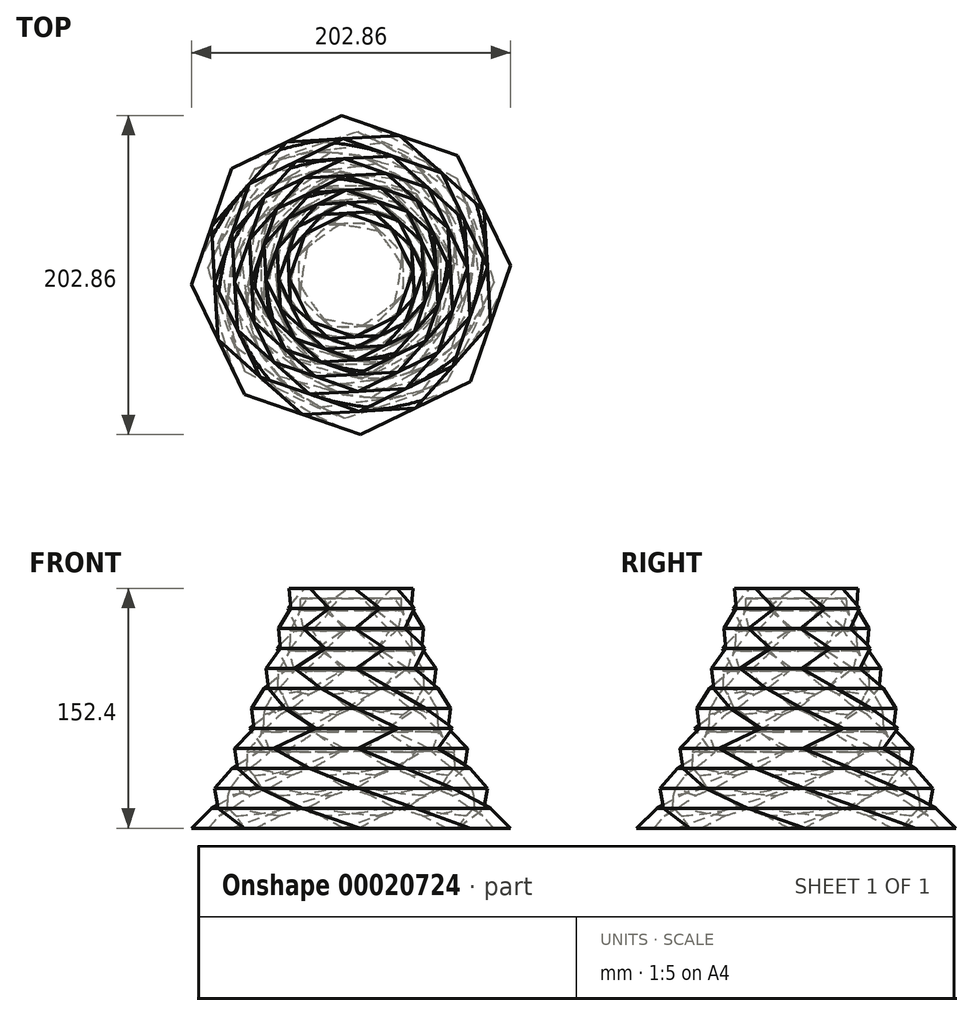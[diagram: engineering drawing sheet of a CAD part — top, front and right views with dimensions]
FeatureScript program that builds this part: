
annotation { "Feature Type Name" : "Feature", "Feature Type Description" : "" }
export const myFeature = defineFeature(function(context is Context, id is Id, definition is map)
    precondition{}
    {
        {
            var Q0;
            Q0=qCreatedBy(makeId("Top.planeOp"),FACE);
            var sketch = newSketch(context, id + "F0", { "sketchPlane" : qUnion([Q0])});
            skCircle(sketch, "E0.cCircle", {"center": v(0, 0) * mm, "radius": 101.6 * mm, "construction": true});
            skLineSegment(sketch, "E0.0", {"start": v(-5.9, 101.43) * mm, "end": v(67.56, 75.89) * mm});
            skLineSegment(sketch, "E0.1", {"start": v(67.56, 75.89) * mm, "end": v(101.43, 5.9) * mm});
            skLineSegment(sketch, "E0.2", {"start": v(101.43, 5.9) * mm, "end": v(75.89, -67.56) * mm});
            skLineSegment(sketch, "E0.3", {"start": v(75.89, -67.56) * mm, "end": v(5.9, -101.43) * mm});
            skLineSegment(sketch, "E0.4", {"start": v(5.9, -101.43) * mm, "end": v(-67.56, -75.89) * mm});
            skLineSegment(sketch, "E0.5", {"start": v(-67.56, -75.89) * mm, "end": v(-101.43, -5.9) * mm});
            skLineSegment(sketch, "E0.6", {"start": v(-101.43, -5.9) * mm, "end": v(-75.89, 67.56) * mm});
            skLineSegment(sketch, "E0.7", {"start": v(-75.89, 67.56) * mm, "end": v(-5.9, 101.43) * mm});
            skSolve(sketch);
        }
        {
            var Q0;
            Q0=qCreatedBy(makeId("Top.planeOp"),FACE);
            cPlane(context, id + "F1", {"entities" : qUnion([Q0]), "cplaneType" : CPlaneType.OFFSET, "offset" : 12.7 * mm, "width" : 152.4 * mm, "height" : 152.4 * mm});
        }
        {
            var Q0;
            Q0=qCreatedBy(id+"F1.planeOp",FACE);
            var sketch = newSketch(context, id + "F2", { "sketchPlane" : qUnion([Q0])});
            skPoint(sketch, "E1.0", {"position": v(-101.43, -5.9) * mm});
            skPoint(sketch, "E2.0", {"position": v(-88.66, 30.83) * mm});
            skCircle(sketch, "E3.cCircle", {"center": v(0, 0) * mm, "radius": 93.87 * mm, "construction": true});
            skLineSegment(sketch, "E3.0", {"start": v(-88.66, 30.83) * mm, "end": v(-40.89, 84.5) * mm});
            skLineSegment(sketch, "E3.1", {"start": v(-40.89, 84.5) * mm, "end": v(30.83, 88.66) * mm});
            skLineSegment(sketch, "E3.2", {"start": v(30.83, 88.66) * mm, "end": v(84.5, 40.89) * mm});
            skLineSegment(sketch, "E3.3", {"start": v(84.5, 40.89) * mm, "end": v(88.66, -30.83) * mm});
            skLineSegment(sketch, "E3.4", {"start": v(88.66, -30.83) * mm, "end": v(40.89, -84.5) * mm});
            skLineSegment(sketch, "E3.5", {"start": v(40.89, -84.5) * mm, "end": v(-30.83, -88.66) * mm});
            skLineSegment(sketch, "E3.6", {"start": v(-30.83, -88.66) * mm, "end": v(-84.5, -40.89) * mm});
            skLineSegment(sketch, "E3.7", {"start": v(-84.5, -40.89) * mm, "end": v(-88.66, 30.83) * mm});
            skSolve(sketch);
        }
        {
            var Q0;
            Q0=makeQuery(id+"F0.imprint","IMPRINT",FACE,{"disambiguationData":[TD([[makeQuery(id+"F0.imprint","IMPRINT",EDGE,{"derivedFrom":sQuery(id+"F0.wireOp",EDGE,"E0.0")}),-1.0]])]});
            var Q1;
            Q1=makeQuery(id+"F2.imprint","IMPRINT",FACE,{"disambiguationData":[TD([[makeQuery(id+"F2.imprint","IMPRINT",EDGE,{"derivedFrom":sQuery(id+"F2.wireOp",EDGE,"E3.0")}),-1.0]])]});
            loft(context, id + "F3", {"sheetProfilesArray" : [{ "sheetProfileEntities" : qUnion([Q0]) }, { "sheetProfileEntities" : qUnion([Q1]) }]});
        }
        {
            var Q0;
            Q0=qCreatedBy(id+"F1.planeOp",FACE);
            cPlane(context, id + "F4", {"entities" : qUnion([Q0]), "cplaneType" : CPlaneType.OFFSET, "offset" : 12.7 * mm, "width" : 152.4 * mm, "height" : 152.4 * mm});
        }
        {
            var Q0;
            Q0=qCreatedBy(id+"F4.planeOp",FACE);
            var sketch = newSketch(context, id + "F5", { "sketchPlane" : qUnion([Q0])});
            skPoint(sketch, "E4.0", {"position": v(0, 0) * mm});
            skPoint(sketch, "E5.0", {"position": v(-86.58, -5.03) * mm});
            skPoint(sketch, "E6.0", {"position": v(-57.66, -64.77) * mm});
            skPoint(sketch, "E7.0", {"position": v(-88.66, 30.83) * mm});
            skCircle(sketch, "E8.cCircle", {"center": v(0, 0) * mm, "radius": 86.72 * mm, "construction": true});
            skLineSegment(sketch, "E8.0", {"start": v(-57.66, -64.77) * mm, "end": v(-86.58, -5.03) * mm});
            skLineSegment(sketch, "E8.1", {"start": v(-86.58, -5.03) * mm, "end": v(-64.77, 57.66) * mm});
            skLineSegment(sketch, "E8.2", {"start": v(-64.77, 57.66) * mm, "end": v(-5.03, 86.58) * mm});
            skLineSegment(sketch, "E8.3", {"start": v(-5.03, 86.58) * mm, "end": v(57.66, 64.77) * mm});
            skLineSegment(sketch, "E8.4", {"start": v(57.66, 64.77) * mm, "end": v(86.58, 5.03) * mm});
            skLineSegment(sketch, "E8.5", {"start": v(86.58, 5.03) * mm, "end": v(64.77, -57.66) * mm});
            skLineSegment(sketch, "E8.6", {"start": v(64.77, -57.66) * mm, "end": v(5.03, -86.58) * mm});
            skLineSegment(sketch, "E8.7", {"start": v(5.03, -86.58) * mm, "end": v(-57.66, -64.77) * mm});
            skSolve(sketch);
        }
        {
            var Q1;
            Q1=makeQuery(id+"F3.opLoft","CAP_FACE",FACE,{"disambiguationData":[OSD([makeQuery(id+"F2.imprint","IMPRINT",FACE,{"disambiguationData":[TD([[makeQuery(id+"F2.imprint","IMPRINT",EDGE,{"derivedFrom":sQuery(id+"F2.wireOp",EDGE,"E3.0")}),-1.0]])]})])],"isStart":true});
            var Q2;
            Q2=makeQuery(id+"F5.imprint","IMPRINT",FACE,{"disambiguationData":[TD([[makeQuery(id+"F5.imprint","IMPRINT",EDGE,{"derivedFrom":sQuery(id+"F5.wireOp",EDGE,"E8.0")}),-1.0]])]});
            loft(context, id + "F6", {"operationType" : NewBodyOperationType.ADD, "sheetProfilesArray" : [{ "sheetProfileEntities" : qUnion([Q1]) }, { "sheetProfileEntities" : qUnion([Q2]) }]});
        }
        {
            var Q0;
            Q0=qCreatedBy(id+"F4.planeOp",FACE);
            cPlane(context, id + "F7", {"entities" : qUnion([Q0]), "cplaneType" : CPlaneType.OFFSET, "offset" : 12.7 * mm, "width" : 152.4 * mm, "height" : 152.4 * mm});
        }
        {
            var Q0;
            Q0=qCreatedBy(id+"F7.planeOp",FACE);
            var sketch = newSketch(context, id + "F8", { "sketchPlane" : qUnion([Q0])});
            skPoint(sketch, "E9.0", {"position": v(26.32, 75.67) * mm});
            skPoint(sketch, "E10.0", {"position": v(0, 0) * mm});
            skCircle(sketch, "E11.cCircle", {"center": v(0, 0) * mm, "radius": 80.12 * mm, "construction": true});
            skLineSegment(sketch, "E11.0", {"start": v(26.32, 75.67) * mm, "end": v(72.12, 34.9) * mm});
            skLineSegment(sketch, "E11.1", {"start": v(72.12, 34.9) * mm, "end": v(75.67, -26.32) * mm});
            skLineSegment(sketch, "E11.2", {"start": v(75.67, -26.32) * mm, "end": v(34.9, -72.12) * mm});
            skLineSegment(sketch, "E11.3", {"start": v(34.9, -72.12) * mm, "end": v(-26.32, -75.67) * mm});
            skLineSegment(sketch, "E11.4", {"start": v(-26.32, -75.67) * mm, "end": v(-72.12, -34.9) * mm});
            skLineSegment(sketch, "E11.5", {"start": v(-72.12, -34.9) * mm, "end": v(-75.67, 26.32) * mm});
            skLineSegment(sketch, "E11.6", {"start": v(-75.67, 26.32) * mm, "end": v(-34.9, 72.12) * mm});
            skLineSegment(sketch, "E11.7", {"start": v(-34.9, 72.12) * mm, "end": v(26.32, 75.67) * mm});
            skSolve(sketch);
        }
        {
            var Q1;
            Q1=makeQuery(id+"F6.opLoft","CAP_FACE",FACE,{"disambiguationData":[OSD([makeQuery(id+"F5.imprint","IMPRINT",FACE,{"disambiguationData":[TD([[makeQuery(id+"F5.imprint","IMPRINT",EDGE,{"derivedFrom":sQuery(id+"F5.wireOp",EDGE,"E8.0")}),-1.0]])]})])],"isStart":true});
            var Q2;
            Q2=makeQuery(id+"F8.imprint","IMPRINT",FACE,{"disambiguationData":[TD([[makeQuery(id+"F8.imprint","IMPRINT",EDGE,{"derivedFrom":sQuery(id+"F8.wireOp",EDGE,"E11.0")}),-1.0]])]});
            loft(context, id + "F9", {"operationType" : NewBodyOperationType.ADD, "sheetProfilesArray" : [{ "sheetProfileEntities" : qUnion([Q1]) }, { "sheetProfileEntities" : qUnion([Q2]) }]});
        }
        {
            var Q0;
            Q0=qCreatedBy(id+"F7.planeOp",FACE);
            cPlane(context, id + "F10", {"entities" : qUnion([Q0]), "cplaneType" : CPlaneType.OFFSET, "offset" : 12.7 * mm, "width" : 152.4 * mm, "height" : 152.4 * mm});
        }
        {
            var Q0;
            Q0=qCreatedBy(id+"F10.planeOp",FACE);
            var sketch = newSketch(context, id + "F11", { "sketchPlane" : qUnion([Q0])});
            skPoint(sketch, "E12.0", {"position": v(0, 0) * mm});
            skPoint(sketch, "E13.0", {"position": v(4.3, -73.9) * mm});
            skCircle(sketch, "E14.cCircle", {"center": v(0, 0) * mm, "radius": 74.02 * mm, "construction": true});
            skLineSegment(sketch, "E14.0", {"start": v(4.3, -73.9) * mm, "end": v(-49.22, -55.29) * mm});
            skLineSegment(sketch, "E14.1", {"start": v(-49.22, -55.29) * mm, "end": v(-73.9, -4.3) * mm});
            skLineSegment(sketch, "E14.2", {"start": v(-73.9, -4.3) * mm, "end": v(-55.29, 49.22) * mm});
            skLineSegment(sketch, "E14.3", {"start": v(-55.29, 49.22) * mm, "end": v(-4.3, 73.9) * mm});
            skLineSegment(sketch, "E14.4", {"start": v(-4.3, 73.9) * mm, "end": v(49.22, 55.29) * mm});
            skLineSegment(sketch, "E14.5", {"start": v(49.22, 55.29) * mm, "end": v(73.9, 4.3) * mm});
            skLineSegment(sketch, "E14.6", {"start": v(73.9, 4.3) * mm, "end": v(55.29, -49.22) * mm});
            skLineSegment(sketch, "E14.7", {"start": v(55.29, -49.22) * mm, "end": v(4.3, -73.9) * mm});
            skSolve(sketch);
        }
        {
            var Q1;
            Q1=makeQuery(id+"F9.opLoft","CAP_FACE",FACE,{"disambiguationData":[OSD([makeQuery(id+"F8.imprint","IMPRINT",FACE,{"disambiguationData":[TD([[makeQuery(id+"F8.imprint","IMPRINT",EDGE,{"derivedFrom":sQuery(id+"F8.wireOp",EDGE,"E11.0")}),-1.0]])]})])],"isStart":true});
            var Q2;
            Q2=makeQuery(id+"F11.imprint","IMPRINT",FACE,{"disambiguationData":[TD([[makeQuery(id+"F11.imprint","IMPRINT",EDGE,{"derivedFrom":sQuery(id+"F11.wireOp",EDGE,"E14.0")}),-1.0]])]});
            loft(context, id + "F12", {"operationType" : NewBodyOperationType.ADD, "sheetProfilesArray" : [{ "sheetProfileEntities" : qUnion([Q1]) }, { "sheetProfileEntities" : qUnion([Q2]) }]});
        }
        {
            var Q0;
            Q0=qCreatedBy(id+"F10.planeOp",FACE);
            cPlane(context, id + "F13", {"entities" : qUnion([Q0]), "cplaneType" : CPlaneType.OFFSET, "offset" : 12.7 * mm, "width" : 152.4 * mm, "height" : 152.4 * mm});
        }
        {
            var Q0;
            Q0=qCreatedBy(id+"F13.planeOp",FACE);
            var sketch = newSketch(context, id + "F14", { "sketchPlane" : qUnion([Q0])});
            skPoint(sketch, "E15.0", {"position": v(0, 0) * mm});
            skPoint(sketch, "E16.0", {"position": v(-22.46, -64.6) * mm});
            skCircle(sketch, "E17.cCircle", {"center": v(0, 0) * mm, "radius": 68.39 * mm, "construction": true});
            skLineSegment(sketch, "E17.0", {"start": v(-22.46, -64.6) * mm, "end": v(-61.56, -29.79) * mm});
            skLineSegment(sketch, "E17.1", {"start": v(-61.56, -29.79) * mm, "end": v(-64.6, 22.46) * mm});
            skLineSegment(sketch, "E17.2", {"start": v(-64.6, 22.46) * mm, "end": v(-29.79, 61.56) * mm});
            skLineSegment(sketch, "E17.3", {"start": v(-29.79, 61.56) * mm, "end": v(22.46, 64.6) * mm});
            skLineSegment(sketch, "E17.4", {"start": v(22.46, 64.6) * mm, "end": v(61.56, 29.79) * mm});
            skLineSegment(sketch, "E17.5", {"start": v(61.56, 29.79) * mm, "end": v(64.6, -22.46) * mm});
            skLineSegment(sketch, "E17.6", {"start": v(64.6, -22.46) * mm, "end": v(29.79, -61.56) * mm});
            skLineSegment(sketch, "E17.7", {"start": v(29.79, -61.56) * mm, "end": v(-22.46, -64.6) * mm});
            skSolve(sketch);
        }
        {
            var Q1;
            Q1=makeQuery(id+"F12.opLoft","CAP_FACE",FACE,{"disambiguationData":[OSD([makeQuery(id+"F11.imprint","IMPRINT",FACE,{"disambiguationData":[TD([[makeQuery(id+"F11.imprint","IMPRINT",EDGE,{"derivedFrom":sQuery(id+"F11.wireOp",EDGE,"E14.0")}),-1.0]])]})])],"isStart":true});
            var Q2;
            Q2=makeQuery(id+"F14.imprint","IMPRINT",FACE,{"disambiguationData":[TD([[makeQuery(id+"F14.imprint","IMPRINT",EDGE,{"derivedFrom":sQuery(id+"F14.wireOp",EDGE,"E17.0")}),-1.0]])]});
            loft(context, id + "F15", {"operationType" : NewBodyOperationType.ADD, "sheetProfilesArray" : [{ "sheetProfileEntities" : qUnion([Q1]) }, { "sheetProfileEntities" : qUnion([Q2]) }]});
        }
        {
            var Q0;
            Q0=qCreatedBy(id+"F13.planeOp",FACE);
            cPlane(context, id + "F16", {"entities" : qUnion([Q0]), "cplaneType" : CPlaneType.OFFSET, "offset" : 12.7 * mm, "width" : 152.4 * mm, "height" : 152.4 * mm});
        }
        {
            var Q0;
            Q0=qCreatedBy(id+"F16.planeOp",FACE);
            var sketch = newSketch(context, id + "F17", { "sketchPlane" : qUnion([Q0])});
            skPoint(sketch, "E18.0", {"position": v(0, 0) * mm});
            skPoint(sketch, "E19.0", {"position": v(3.66, -63.07) * mm});
            skCircle(sketch, "E20.cCircle", {"center": v(0, 0) * mm, "radius": 63.18 * mm, "construction": true});
            skLineSegment(sketch, "E20.0", {"start": v(3.66, -63.07) * mm, "end": v(-42, -47.2) * mm});
            skLineSegment(sketch, "E20.1", {"start": v(-42, -47.2) * mm, "end": v(-63.07, -3.66) * mm});
            skLineSegment(sketch, "E20.2", {"start": v(-63.07, -3.66) * mm, "end": v(-47.2, 42) * mm});
            skLineSegment(sketch, "E20.3", {"start": v(-47.2, 42) * mm, "end": v(-3.66, 63.07) * mm});
            skLineSegment(sketch, "E20.4", {"start": v(-3.66, 63.07) * mm, "end": v(42, 47.2) * mm});
            skLineSegment(sketch, "E20.5", {"start": v(42, 47.2) * mm, "end": v(63.07, 3.66) * mm});
            skLineSegment(sketch, "E20.6", {"start": v(63.07, 3.66) * mm, "end": v(47.2, -42) * mm});
            skLineSegment(sketch, "E20.7", {"start": v(47.2, -42) * mm, "end": v(3.66, -63.07) * mm});
            skSolve(sketch);
        }
        {
            var Q1;
            Q1=makeQuery(id+"F15.opLoft","CAP_FACE",FACE,{"disambiguationData":[OSD([makeQuery(id+"F14.imprint","IMPRINT",FACE,{"disambiguationData":[TD([[makeQuery(id+"F14.imprint","IMPRINT",EDGE,{"derivedFrom":sQuery(id+"F14.wireOp",EDGE,"E17.0")}),-1.0]])]})])],"isStart":true});
            var Q2;
            Q2=makeQuery(id+"F17.imprint","IMPRINT",FACE,{"disambiguationData":[TD([[makeQuery(id+"F17.imprint","IMPRINT",EDGE,{"derivedFrom":sQuery(id+"F17.wireOp",EDGE,"E20.0")}),-1.0]])]});
            loft(context, id + "F18", {"operationType" : NewBodyOperationType.ADD, "sheetProfilesArray" : [{ "sheetProfileEntities" : qUnion([Q1]) }, { "sheetProfileEntities" : qUnion([Q2]) }]});
        }
        {
            var Q0;
            Q0=qCreatedBy(id+"F16.planeOp",FACE);
            cPlane(context, id + "F19", {"entities" : qUnion([Q0]), "cplaneType" : CPlaneType.OFFSET, "offset" : 12.7 * mm, "width" : 152.4 * mm, "height" : 152.4 * mm});
        }
        {
            var Q0;
            Q0=qCreatedBy(id+"F19.planeOp",FACE);
            var sketch = newSketch(context, id + "F20", { "sketchPlane" : qUnion([Q0])});
            skPoint(sketch, "E21.0", {"position": v(0, 0) * mm});
            skPoint(sketch, "E22.0", {"position": v(25.43, -52.54) * mm});
            skCircle(sketch, "E23.cCircle", {"center": v(0, 0) * mm, "radius": 58.37 * mm, "construction": true});
            skLineSegment(sketch, "E23.0", {"start": v(25.43, -52.54) * mm, "end": v(-19.17, -55.13) * mm});
            skLineSegment(sketch, "E23.1", {"start": v(-19.17, -55.13) * mm, "end": v(-52.54, -25.43) * mm});
            skLineSegment(sketch, "E23.2", {"start": v(-52.54, -25.43) * mm, "end": v(-55.13, 19.17) * mm});
            skLineSegment(sketch, "E23.3", {"start": v(-55.13, 19.17) * mm, "end": v(-25.43, 52.54) * mm});
            skLineSegment(sketch, "E23.4", {"start": v(-25.43, 52.54) * mm, "end": v(19.17, 55.13) * mm});
            skLineSegment(sketch, "E23.5", {"start": v(19.17, 55.13) * mm, "end": v(52.54, 25.43) * mm});
            skLineSegment(sketch, "E23.6", {"start": v(52.54, 25.43) * mm, "end": v(55.13, -19.17) * mm});
            skLineSegment(sketch, "E23.7", {"start": v(55.13, -19.17) * mm, "end": v(25.43, -52.54) * mm});
            skSolve(sketch);
        }
        {
            var Q1;
            Q1=makeQuery(id+"F18.opLoft","CAP_FACE",FACE,{"disambiguationData":[OSD([makeQuery(id+"F17.imprint","IMPRINT",FACE,{"disambiguationData":[TD([[makeQuery(id+"F17.imprint","IMPRINT",EDGE,{"derivedFrom":sQuery(id+"F17.wireOp",EDGE,"E20.0")}),-1.0]])]})])],"isStart":true});
            var Q2;
            Q2=makeQuery(id+"F20.imprint","IMPRINT",FACE,{"disambiguationData":[TD([[makeQuery(id+"F20.imprint","IMPRINT",EDGE,{"derivedFrom":sQuery(id+"F20.wireOp",EDGE,"E23.0")}),-1.0]])]});
            loft(context, id + "F21", {"operationType" : NewBodyOperationType.ADD, "sheetProfilesArray" : [{ "sheetProfileEntities" : qUnion([Q1]) }, { "sheetProfileEntities" : qUnion([Q2]) }]});
        }
        {
            var Q0;
            Q0=qCreatedBy(id+"F19.planeOp",FACE);
            cPlane(context, id + "F22", {"entities" : qUnion([Q0]), "cplaneType" : CPlaneType.OFFSET, "offset" : 12.7 * mm, "width" : 152.4 * mm, "height" : 152.4 * mm});
        }
        {
            var Q0;
            Q0=qCreatedBy(id+"F22.planeOp",FACE);
            var sketch = newSketch(context, id + "F23", { "sketchPlane" : qUnion([Q0])});
            skPoint(sketch, "E24.0", {"position": v(0, 0) * mm});
            skPoint(sketch, "E25.0", {"position": v(3.13, -53.84) * mm});
            skCircle(sketch, "E26.cCircle", {"center": v(0, 0) * mm, "radius": 53.93 * mm, "construction": true});
            skLineSegment(sketch, "E26.0", {"start": v(3.13, -53.84) * mm, "end": v(-35.86, -40.28) * mm});
            skLineSegment(sketch, "E26.1", {"start": v(-35.86, -40.28) * mm, "end": v(-53.84, -3.13) * mm});
            skLineSegment(sketch, "E26.2", {"start": v(-53.84, -3.13) * mm, "end": v(-40.28, 35.86) * mm});
            skLineSegment(sketch, "E26.3", {"start": v(-40.28, 35.86) * mm, "end": v(-3.13, 53.84) * mm});
            skLineSegment(sketch, "E26.4", {"start": v(-3.13, 53.84) * mm, "end": v(35.86, 40.28) * mm});
            skLineSegment(sketch, "E26.5", {"start": v(35.86, 40.28) * mm, "end": v(53.84, 3.13) * mm});
            skLineSegment(sketch, "E26.6", {"start": v(53.84, 3.13) * mm, "end": v(40.28, -35.86) * mm});
            skLineSegment(sketch, "E26.7", {"start": v(40.28, -35.86) * mm, "end": v(3.13, -53.84) * mm});
            skSolve(sketch);
        }
        {
            var Q1;
            Q1=makeQuery(id+"F21.opLoft","CAP_FACE",FACE,{"disambiguationData":[OSD([makeQuery(id+"F20.imprint","IMPRINT",FACE,{"disambiguationData":[TD([[makeQuery(id+"F20.imprint","IMPRINT",EDGE,{"derivedFrom":sQuery(id+"F20.wireOp",EDGE,"E23.0")}),-1.0]])]})])],"isStart":true});
            var Q2;
            Q2=makeQuery(id+"F23.imprint","IMPRINT",FACE,{"disambiguationData":[TD([[makeQuery(id+"F23.imprint","IMPRINT",EDGE,{"derivedFrom":sQuery(id+"F23.wireOp",EDGE,"E26.0")}),-1.0]])]});
            loft(context, id + "F24", {"operationType" : NewBodyOperationType.ADD, "sheetProfilesArray" : [{ "sheetProfileEntities" : qUnion([Q1]) }, { "sheetProfileEntities" : qUnion([Q2]) }]});
        }
        {
            var Q0;
            Q0=qCreatedBy(id+"F22.planeOp",FACE);
            cPlane(context, id + "F25", {"entities" : qUnion([Q0]), "cplaneType" : CPlaneType.OFFSET, "offset" : 12.7 * mm, "width" : 152.4 * mm, "height" : 152.4 * mm});
        }
        {
            var Q0;
            Q0=qCreatedBy(id+"F25.planeOp",FACE);
            var sketch = newSketch(context, id + "F26", { "sketchPlane" : qUnion([Q0])});
            skPoint(sketch, "E27.0", {"position": v(0, 0) * mm});
            skPoint(sketch, "E28.0", {"position": v(-16.37, -47.06) * mm});
            skCircle(sketch, "E29.cCircle", {"center": v(0, 0) * mm, "radius": 49.82 * mm, "construction": true});
            skLineSegment(sketch, "E29.0", {"start": v(-16.37, -47.06) * mm, "end": v(-44.85, -21.7) * mm});
            skLineSegment(sketch, "E29.1", {"start": v(-44.85, -21.7) * mm, "end": v(-47.06, 16.37) * mm});
            skLineSegment(sketch, "E29.2", {"start": v(-47.06, 16.37) * mm, "end": v(-21.7, 44.85) * mm});
            skLineSegment(sketch, "E29.3", {"start": v(-21.7, 44.85) * mm, "end": v(16.37, 47.06) * mm});
            skLineSegment(sketch, "E29.4", {"start": v(16.37, 47.06) * mm, "end": v(44.85, 21.7) * mm});
            skLineSegment(sketch, "E29.5", {"start": v(44.85, 21.7) * mm, "end": v(47.06, -16.37) * mm});
            skLineSegment(sketch, "E29.6", {"start": v(47.06, -16.37) * mm, "end": v(21.7, -44.85) * mm});
            skLineSegment(sketch, "E29.7", {"start": v(21.7, -44.85) * mm, "end": v(-16.37, -47.06) * mm});
            skSolve(sketch);
        }
        {
            var Q1;
            Q1=makeQuery(id+"F24.opLoft","CAP_FACE",FACE,{"disambiguationData":[OSD([makeQuery(id+"F23.imprint","IMPRINT",FACE,{"disambiguationData":[TD([[makeQuery(id+"F23.imprint","IMPRINT",EDGE,{"derivedFrom":sQuery(id+"F23.wireOp",EDGE,"E26.0")}),-1.0]])]})])],"isStart":true});
            var Q2;
            Q2=makeQuery(id+"F26.imprint","IMPRINT",FACE,{"disambiguationData":[TD([[makeQuery(id+"F26.imprint","IMPRINT",EDGE,{"derivedFrom":sQuery(id+"F26.wireOp",EDGE,"E29.0")}),-1.0]])]});
            loft(context, id + "F27", {"operationType" : NewBodyOperationType.ADD, "sheetProfilesArray" : [{ "sheetProfileEntities" : qUnion([Q1]) }, { "sheetProfileEntities" : qUnion([Q2]) }]});
        }
        {
            var Q0;
            Q0=qCreatedBy(id+"F25.planeOp",FACE);
            cPlane(context, id + "F28", {"entities" : qUnion([Q0]), "cplaneType" : CPlaneType.OFFSET, "offset" : 12.7 * mm, "width" : 152.4 * mm, "height" : 152.4 * mm});
        }
        {
            var Q0;
            Q0=qCreatedBy(id+"F28.planeOp",FACE);
            var sketch = newSketch(context, id + "F29", { "sketchPlane" : qUnion([Q0])});
            skPoint(sketch, "E30.0", {"position": v(0, 0) * mm});
            skPoint(sketch, "E31.0", {"position": v(2.67, -45.95) * mm});
            skCircle(sketch, "E32.cCircle", {"center": v(0, 0) * mm, "radius": 46.03 * mm, "construction": true});
            skLineSegment(sketch, "E32.0", {"start": v(2.67, -45.95) * mm, "end": v(-30.6, -34.38) * mm});
            skLineSegment(sketch, "E32.1", {"start": v(-30.6, -34.38) * mm, "end": v(-45.95, -2.67) * mm});
            skLineSegment(sketch, "E32.2", {"start": v(-45.95, -2.67) * mm, "end": v(-34.38, 30.6) * mm});
            skLineSegment(sketch, "E32.3", {"start": v(-34.38, 30.6) * mm, "end": v(-2.67, 45.95) * mm});
            skLineSegment(sketch, "E32.4", {"start": v(-2.67, 45.95) * mm, "end": v(30.6, 34.38) * mm});
            skLineSegment(sketch, "E32.5", {"start": v(30.6, 34.38) * mm, "end": v(45.95, 2.67) * mm});
            skLineSegment(sketch, "E32.6", {"start": v(45.95, 2.67) * mm, "end": v(34.38, -30.6) * mm});
            skLineSegment(sketch, "E32.7", {"start": v(34.38, -30.6) * mm, "end": v(2.67, -45.95) * mm});
            skSolve(sketch);
        }
        {
            var Q1;
            Q1=makeQuery(id+"F27.opLoft","CAP_FACE",FACE,{"disambiguationData":[OSD([makeQuery(id+"F26.imprint","IMPRINT",FACE,{"disambiguationData":[TD([[makeQuery(id+"F26.imprint","IMPRINT",EDGE,{"derivedFrom":sQuery(id+"F26.wireOp",EDGE,"E29.0")}),-1.0]])]})])],"isStart":true});
            var Q2;
            Q2=makeQuery(id+"F29.imprint","IMPRINT",FACE,{"disambiguationData":[TD([[makeQuery(id+"F29.imprint","IMPRINT",EDGE,{"derivedFrom":sQuery(id+"F29.wireOp",EDGE,"E32.0")}),-1.0]])]});
            loft(context, id + "F30", {"operationType" : NewBodyOperationType.ADD, "sheetProfilesArray" : [{ "sheetProfileEntities" : qUnion([Q1]) }, { "sheetProfileEntities" : qUnion([Q2]) }]});
        }
        {
            var Q0;
            Q0=qCreatedBy(id+"F28.planeOp",FACE);
            cPlane(context, id + "F31", {"entities" : qUnion([Q0]), "cplaneType" : CPlaneType.OFFSET, "offset" : 12.7 * mm, "width" : 152.4 * mm, "height" : 152.4 * mm});
        }
        {
            var Q0;
            Q0=qCreatedBy(id+"F31.planeOp",FACE);
            var sketch = newSketch(context, id + "F32", { "sketchPlane" : qUnion([Q0])});
            skPoint(sketch, "E33.0", {"position": v(0, 0) * mm});
            skPoint(sketch, "E34.0", {"position": v(-13.97, -40.17) * mm});
            skCircle(sketch, "E35.cCircle", {"center": v(0, 0) * mm, "radius": 42.53 * mm, "construction": true});
            skLineSegment(sketch, "E35.0", {"start": v(-13.97, -40.17) * mm, "end": v(-38.28, -18.53) * mm});
            skLineSegment(sketch, "E35.1", {"start": v(-38.28, -18.53) * mm, "end": v(-40.17, 13.97) * mm});
            skLineSegment(sketch, "E35.2", {"start": v(-40.17, 13.97) * mm, "end": v(-18.53, 38.28) * mm});
            skLineSegment(sketch, "E35.3", {"start": v(-18.53, 38.28) * mm, "end": v(13.97, 40.17) * mm});
            skLineSegment(sketch, "E35.4", {"start": v(13.97, 40.17) * mm, "end": v(38.28, 18.53) * mm});
            skLineSegment(sketch, "E35.5", {"start": v(38.28, 18.53) * mm, "end": v(40.17, -13.97) * mm});
            skLineSegment(sketch, "E35.6", {"start": v(40.17, -13.97) * mm, "end": v(18.53, -38.28) * mm});
            skLineSegment(sketch, "E35.7", {"start": v(18.53, -38.28) * mm, "end": v(-13.97, -40.17) * mm});
            skSolve(sketch);
        }
        {
            var Q1;
            Q1=makeQuery(id+"F30.opLoft","CAP_FACE",FACE,{"disambiguationData":[OSD([makeQuery(id+"F29.imprint","IMPRINT",FACE,{"disambiguationData":[TD([[makeQuery(id+"F29.imprint","IMPRINT",EDGE,{"derivedFrom":sQuery(id+"F29.wireOp",EDGE,"E32.0")}),-1.0]])]})])],"isStart":true});
            var Q2;
            Q2=makeQuery(id+"F32.imprint","IMPRINT",FACE,{"disambiguationData":[TD([[makeQuery(id+"F32.imprint","IMPRINT",EDGE,{"derivedFrom":sQuery(id+"F32.wireOp",EDGE,"E35.0")}),-1.0]])]});
            loft(context, id + "F33", {"operationType" : NewBodyOperationType.ADD, "sheetProfilesArray" : [{ "sheetProfileEntities" : qUnion([Q1]) }, { "sheetProfileEntities" : qUnion([Q2]) }]});
        }
        {
            var Q0;
            Q0=qCreatedBy(id+"F31.planeOp",FACE);
            cPlane(context, id + "F34", {"entities" : qUnion([Q0]), "cplaneType" : CPlaneType.OFFSET, "offset" : 12.7 * mm, "width" : 152.4 * mm, "height" : 152.4 * mm});
        }
        {
            var Q0;
            Q0=qCreatedBy(id+"F34.planeOp",FACE);
            var sketch = newSketch(context, id + "F35", { "sketchPlane" : qUnion([Q0])});
            skPoint(sketch, "E36.0", {"position": v(0, 0) * mm});
            skPoint(sketch, "E37.0", {"position": v(-26.12, -29.35) * mm});
            skCircle(sketch, "E38.cCircle", {"center": v(0, 0) * mm, "radius": 39.29 * mm, "construction": true});
            skLineSegment(sketch, "E38.0", {"start": v(-26.12, -29.35) * mm, "end": v(-39.22, -2.28) * mm});
            skLineSegment(sketch, "E38.1", {"start": v(-39.22, -2.28) * mm, "end": v(-29.35, 26.12) * mm});
            skLineSegment(sketch, "E38.2", {"start": v(-29.35, 26.12) * mm, "end": v(-2.28, 39.22) * mm});
            skLineSegment(sketch, "E38.3", {"start": v(-2.28, 39.22) * mm, "end": v(26.12, 29.35) * mm});
            skLineSegment(sketch, "E38.4", {"start": v(26.12, 29.35) * mm, "end": v(39.22, 2.28) * mm});
            skLineSegment(sketch, "E38.5", {"start": v(39.22, 2.28) * mm, "end": v(29.35, -26.12) * mm});
            skLineSegment(sketch, "E38.6", {"start": v(29.35, -26.12) * mm, "end": v(2.28, -39.22) * mm});
            skLineSegment(sketch, "E38.7", {"start": v(2.28, -39.22) * mm, "end": v(-26.12, -29.35) * mm});
            skSolve(sketch);
        }
        {
            var Q1;
            Q1=makeQuery(id+"F33.opLoft","CAP_FACE",FACE,{"disambiguationData":[OSD([makeQuery(id+"F32.imprint","IMPRINT",FACE,{"disambiguationData":[TD([[makeQuery(id+"F32.imprint","IMPRINT",EDGE,{"derivedFrom":sQuery(id+"F32.wireOp",EDGE,"E35.0")}),-1.0]])]})])],"isStart":true});
            var Q2;
            Q2=makeQuery(id+"F35.imprint","IMPRINT",FACE,{"disambiguationData":[TD([[makeQuery(id+"F35.imprint","IMPRINT",EDGE,{"derivedFrom":sQuery(id+"F35.wireOp",EDGE,"E38.0")}),-1.0]])]});
            loft(context, id + "F36", {"operationType" : NewBodyOperationType.ADD, "sheetProfilesArray" : [{ "sheetProfileEntities" : qUnion([Q1]) }, { "sheetProfileEntities" : qUnion([Q2]) }]});
        }
        {
            var Q0;
            Q0=makeQuery(id+"F3.opLoft","CAP_FACE",FACE,{"disambiguationData":[OSD([makeQuery(id+"F0.imprint","IMPRINT",FACE,{"disambiguationData":[TD([[makeQuery(id+"F0.imprint","IMPRINT",EDGE,{"derivedFrom":sQuery(id+"F0.wireOp",EDGE,"E0.0")}),-1.0]])]})])],"isStart":true});
            shell(context, id + "F37", {"entities" : qUnion([Q0]), "thickness" : 6.35 * mm});
        }
    });
